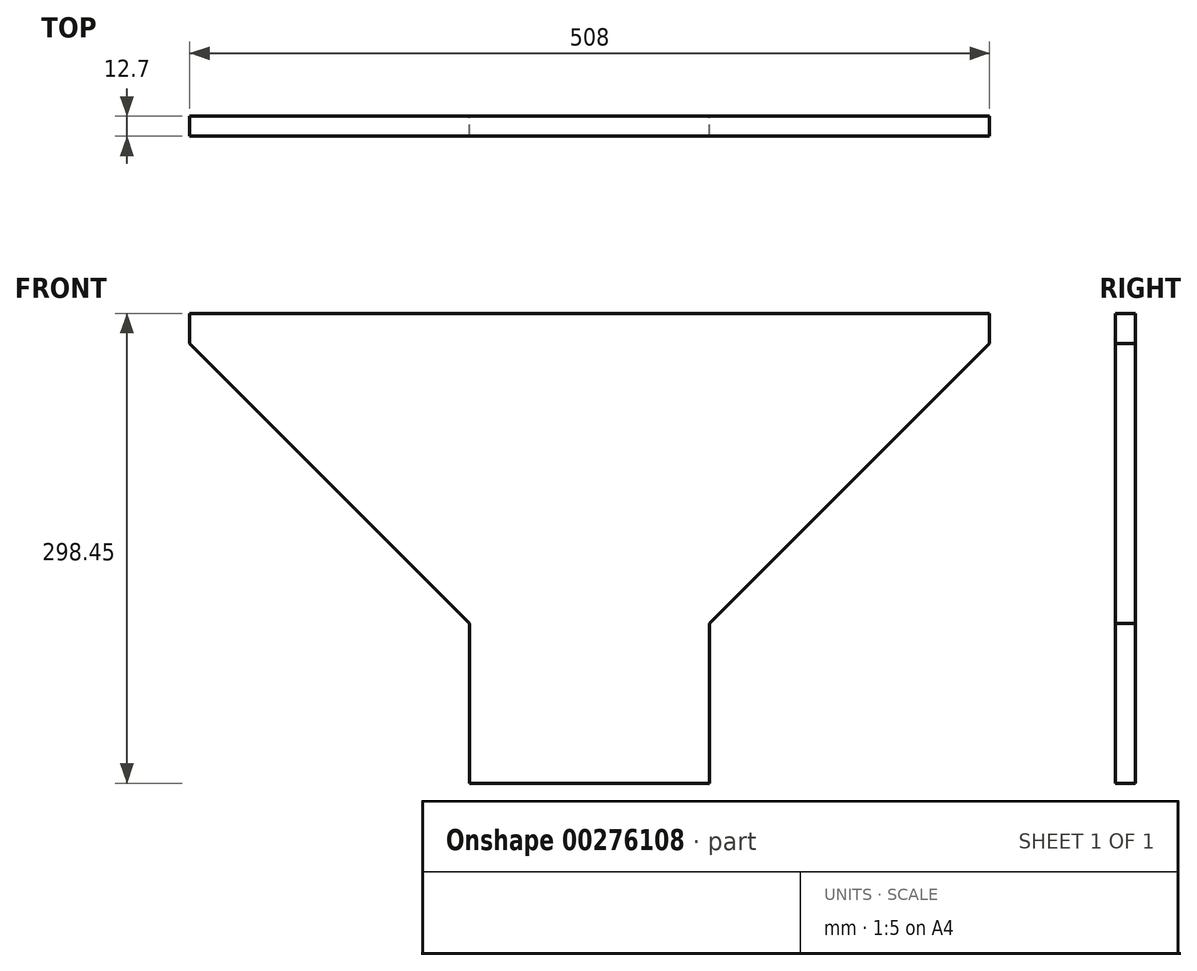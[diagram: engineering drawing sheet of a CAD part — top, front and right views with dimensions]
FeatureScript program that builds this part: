
annotation { "Feature Type Name" : "Feature", "Feature Type Description" : "" }
export const myFeature = defineFeature(function(context is Context, id is Id, definition is map)
    precondition{}
    {
        {
            var Q0;
            Q0=qCreatedBy(makeId("Front.planeOp"),FACE);
            var sketch = newSketch(context, id + "F0", { "sketchPlane" : qUnion([Q0])});
            skLineSegment(sketch, "E0", {"start": v(254, 0) * mm, "end": v(50.8, -203.2) * mm});
            skLineSegment(sketch, "E1", {"start": v(-254, 0) * mm, "end": v(-50.8, -203.2) * mm});
            skArc(sketch, "E2", {"start": v(50.8, -203.2) * mm, "mid": v(0, -254) * mm, "end": v(-50.8, -203.2) * mm, "construction": true});
            skLineSegment(sketch, "E3", {"start": v(0, -203.2) * mm, "end": v(-187.32, -203.2) * mm, "construction": true});
            skLineSegment(sketch, "E4", {"start": v(0, -203.2) * mm, "end": v(193.28, -203.2) * mm, "construction": true});
            skLineSegment(sketch, "E5", {"start": v(-254, 0) * mm, "end": v(254, 0) * mm, "construction": true});
            skLineSegment(sketch, "E6", {"start": v(-254, 0) * mm, "end": v(-254, 19.05) * mm});
            skLineSegment(sketch, "E7", {"start": v(-254, 19.05) * mm, "end": v(254, 19.05) * mm});
            skLineSegment(sketch, "E8", {"start": v(254, 19.05) * mm, "end": v(254, 0) * mm});
            skLineSegment(sketch, "E9", {"start": v(-76.2, -177.8) * mm, "end": v(-76.2, -279.4) * mm});
            skLineSegment(sketch, "E10", {"start": v(-76.2, -279.4) * mm, "end": v(76.2, -279.4) * mm});
            skLineSegment(sketch, "E11", {"start": v(76.2, -279.4) * mm, "end": v(76.2, -177.8) * mm});
            skSolve(sketch);
        }
        {
            var Q0;
            {var subQ0=sQuery(id+"F0.wireOp",EDGE,"E6");Q0=makeQuery(id+"F0.imprint","IMPRINT",FACE,{"disambiguationData":[TD([[makeQuery(id+"F0.imprint","IMPRINT",EDGE,{"derivedFrom":subQ0}),-1.0]])]});}
            extrude(context, id + "F1", {"entities" : qUnion([Q0]), "depth" : 12.7 * mm});
        }
    });
